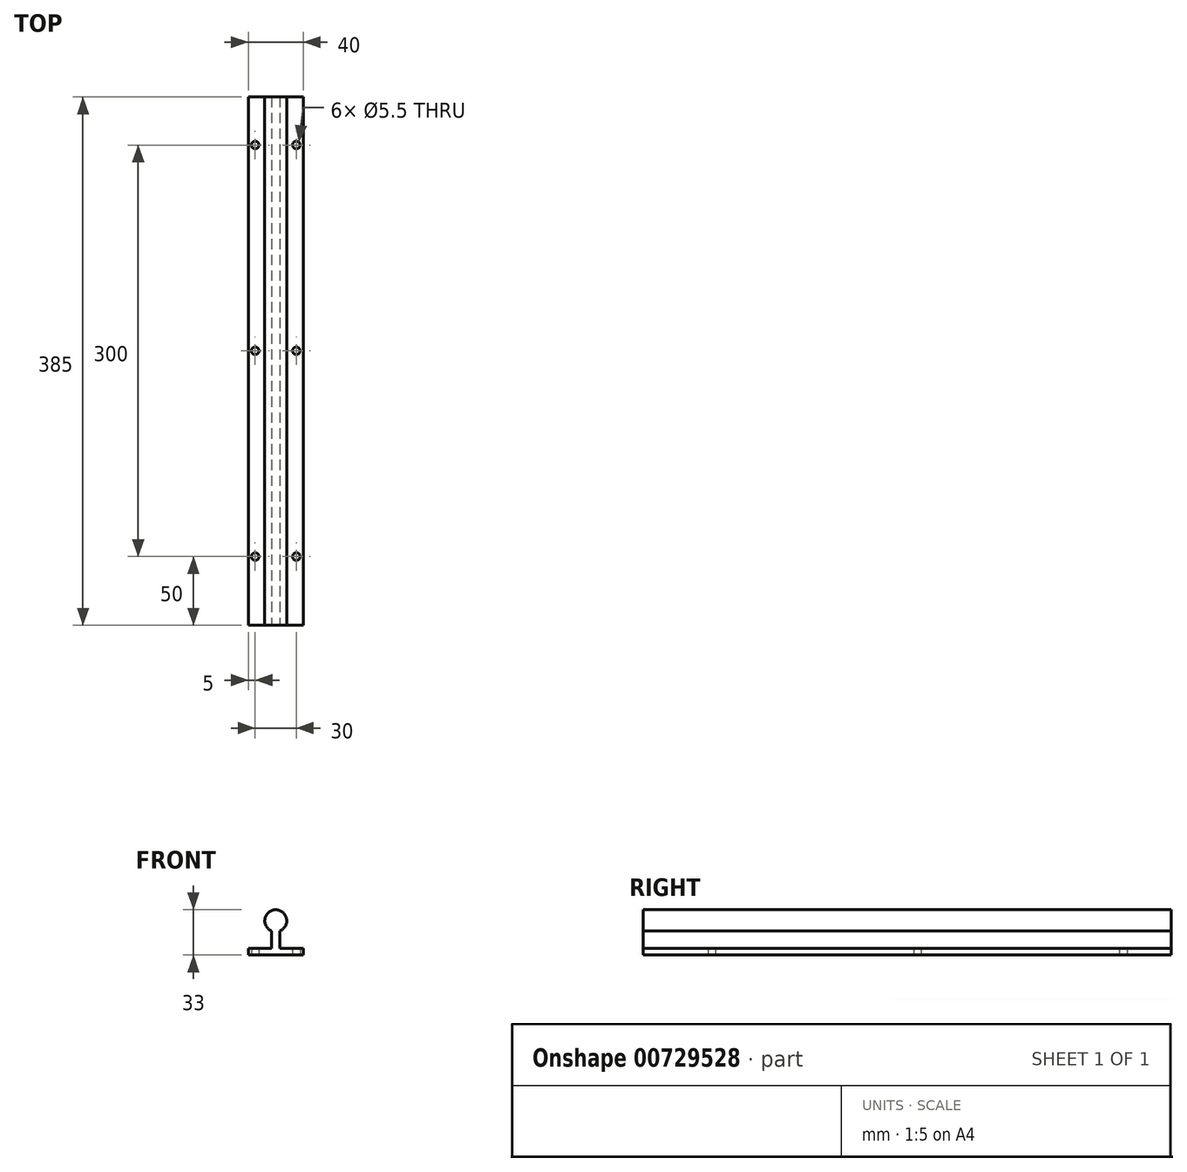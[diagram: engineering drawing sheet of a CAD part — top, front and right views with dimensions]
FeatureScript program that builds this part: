
annotation { "Feature Type Name" : "Feature", "Feature Type Description" : "" }
export const myFeature = defineFeature(function(context is Context, id is Id, definition is map)
    precondition{}
    {
        {
            var Q0;
            Q0=qCreatedBy(makeId("Front.planeOp"),FACE);
            var sketch = newSketch(context, id + "F0", { "sketchPlane" : qUnion([Q0])});
            skLineSegment(sketch, "E0.bottom", {"start": v(20, 2.5) * mm, "end": v(3, 2.5) * mm});
            skLineSegment(sketch, "E0.top", {"start": v(20, -2.5) * mm, "end": v(-20, -2.5) * mm});
            skLineSegment(sketch, "E0.left", {"start": v(20, 2.5) * mm, "end": v(20, -2.5) * mm});
            skLineSegment(sketch, "E0.right", {"start": v(-20, 2.5) * mm, "end": v(-20, -2.5) * mm});
            skPoint(sketch, "E0.middle", {"position": v(0, 0) * mm});
            skLineSegment(sketch, "E1.left", {"start": v(-3, 2.5) * mm, "end": v(-3, 15.08) * mm});
            skLineSegment(sketch, "E1.right", {"start": v(3, 2.5) * mm, "end": v(3, 15.08) * mm});
            skLineSegment(sketch, "E2", {"start": v(0, 50.09) * mm, "end": v(0, -27) * mm, "construction": true});
            skArc(sketch, "E3", {"start": v(3, 15.08) * mm, "mid": v(0, 30.5) * mm, "end": v(-3, 15.08) * mm});
            skLineSegment(sketch, "E4.trimOffspring", {"start": v(-3, 2.5) * mm, "end": v(-20, 2.5) * mm});
            skSolve(sketch);
        }
        {
            var Q0;
            Q0=qCreatedBy(makeId("Top.planeOp"),FACE);
            var sketch = newSketch(context, id + "F1", { "sketchPlane" : qUnion([Q0])});
            skLineSegment(sketch, "E5", {"start": v(-20, 0) * mm, "end": v(-20, 385) * mm});
            skLineSegment(sketch, "E6", {"start": v(-20, 385) * mm, "end": v(20, 385) * mm});
            skLineSegment(sketch, "E7", {"start": v(20, 385) * mm, "end": v(20, 0) * mm});
            skLineSegment(sketch, "E8", {"start": v(15, 2225.2) * mm, "end": v(15, -705.2) * mm, "construction": true});
            skCircle(sketch, "E9", {"center": v(15, 50) * mm, "radius": 2.75 * mm});
            skCircle(sketch, "E10", {"center": v(15, 200) * mm, "radius": 2.75 * mm});
            skCircle(sketch, "E11", {"center": v(15, 350) * mm, "radius": 2.75 * mm});
            skLineSegment(sketch, "E12", {"start": v(0, 654.2) * mm, "end": v(0, 0) * mm, "construction": true});
            skLineSegment(sketch, "E13.MirrorCS", {"start": v(-15, 2225.2) * mm, "end": v(-15, -705.2) * mm, "construction": true});
            skCircle(sketch, "E14.MirrorC", {"center": v(-15, 50) * mm, "radius": 2.75 * mm});
            skCircle(sketch, "E15.MirrorC", {"center": v(-15, 200) * mm, "radius": 2.75 * mm});
            skCircle(sketch, "E16.MirrorC", {"center": v(-15, 350) * mm, "radius": 2.75 * mm});
            skSolve(sketch);
        }
        {
            var Q0;
            Q0 = qSketchRegion(id + "F0", true);
            extrude(context, id + "F2", {"entities" : qUnion([Q0]), "oppositeDirection" : true, "depth" : 385 * mm, "offsetDistance" : 25 * mm});
        }
        {
            var Q0;
            Q0 = qSketchRegion(id + "F1", true);
            extrude(context, id + "F3", {"entities" : qUnion([Q0]), "operationType" : NewBodyOperationType.REMOVE, "depth" : 5.5 * mm, "offsetDistance" : 25 * mm, "symmetric" : true});
        }
    });
